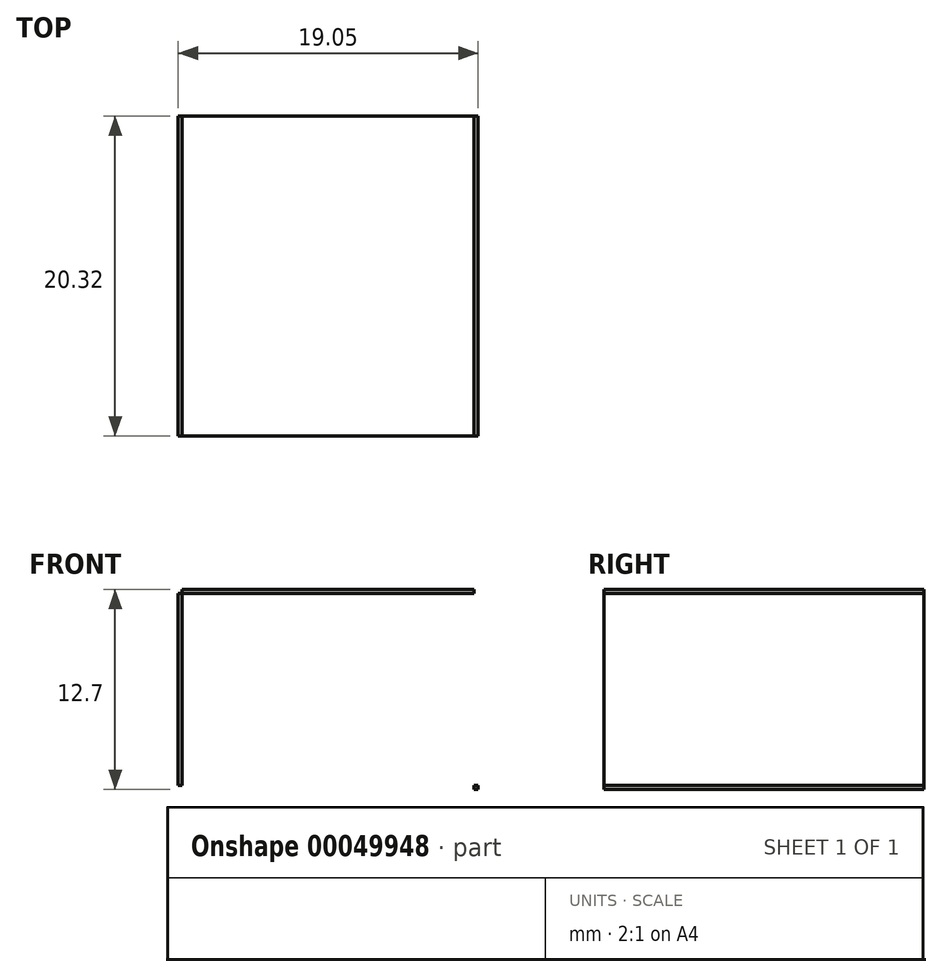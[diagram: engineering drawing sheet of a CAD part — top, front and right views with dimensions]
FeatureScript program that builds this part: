
annotation { "Feature Type Name" : "Feature", "Feature Type Description" : "" }
export const myFeature = defineFeature(function(context is Context, id is Id, definition is map)
    precondition{}
    {
        {
            var Q0;
            Q0=qCreatedBy(makeId("Front.planeOp"),FACE);
            var sketch = newSketch(context, id + "F0", { "sketchPlane" : qUnion([Q0])});
            skLineSegment(sketch, "E0", {"start": v(0, 0) * mm, "end": v(19.05, 0) * mm});
            skLineSegment(sketch, "E1", {"start": v(19.05, 0) * mm, "end": v(19.05, 12.7) * mm});
            skLineSegment(sketch, "E2", {"start": v(19.05, 12.7) * mm, "end": v(0, 12.7) * mm});
            skLineSegment(sketch, "E3", {"start": v(0, 12.7) * mm, "end": v(0, 0) * mm});
            skLineSegment(sketch, "E4", {"start": v(0, 0) * mm, "end": v(0.25, 0) * mm});
            skLineSegment(sketch, "E5", {"start": v(0.25, 0) * mm, "end": v(0.25, 0.25) * mm});
            skLineSegment(sketch, "E6", {"start": v(0.25, 0.25) * mm, "end": v(0, 0.25) * mm});
            skLineSegment(sketch, "E7", {"start": v(0, 12.7) * mm, "end": v(0, 12.45) * mm});
            skLineSegment(sketch, "E8", {"start": v(0, 12.45) * mm, "end": v(0.25, 12.45) * mm});
            skLineSegment(sketch, "E9", {"start": v(0.25, 12.45) * mm, "end": v(0.25, 12.7) * mm});
            skLineSegment(sketch, "E10", {"start": v(0.25, 12.45) * mm, "end": v(0.25, 0.25) * mm});
            skLineSegment(sketch, "E11", {"start": v(19.05, 12.7) * mm, "end": v(18.8, 12.7) * mm});
            skLineSegment(sketch, "E12", {"start": v(18.8, 12.7) * mm, "end": v(18.8, 12.45) * mm});
            skLineSegment(sketch, "E13", {"start": v(18.8, 12.45) * mm, "end": v(0.25, 12.45) * mm});
            skLineSegment(sketch, "E14", {"start": v(19.05, 0.25) * mm, "end": v(18.8, 0.25) * mm});
            skLineSegment(sketch, "E15", {"start": v(18.8, 0.25) * mm, "end": v(18.8, 0) * mm});
            skLineSegment(sketch, "E16", {"start": v(18.8, 0.25) * mm, "end": v(18.8, 12.45) * mm});
            skSolve(sketch);
        }
        {
            var Q0;
            {var subQ4=sQuery(id+"F0.wireOp",EDGE,"E14");Q0=makeQuery(id+"F0.imprint","IMPRINT",FACE,{"disambiguationData":[TD([[makeQuery(id+"F0.imprint","IMPRINT",EDGE,{"derivedFrom":subQ4}),1.0]])]});}
            var Q1;
            {var subQ0=sQuery(id+"F0.wireOp",EDGE,"E7");Q1=makeQuery(id+"F0.imprint","IMPRINT",FACE,{"disambiguationData":[TD([[makeQuery(id+"F0.imprint","IMPRINT",EDGE,{"derivedFrom":subQ0}),1.0]])]});}
            var Q2;
            {var subQ0=sQuery(id+"F0.wireOp",EDGE,"E4");Q2=makeQuery(id+"F0.imprint","IMPRINT",FACE,{"disambiguationData":[TD([[makeQuery(id+"F0.imprint","IMPRINT",EDGE,{"derivedFrom":subQ0}),1.0]])]});}
            var Q3;
            {var subQ0=sQuery(id+"F0.wireOp",EDGE,"E11");Q3=makeQuery(id+"F0.imprint","IMPRINT",FACE,{"disambiguationData":[TD([[makeQuery(id+"F0.imprint","IMPRINT",EDGE,{"derivedFrom":subQ0}),1.0]])]});}
            var Q4;
            {var subQ2=sQuery(id+"F0.wireOp",EDGE,"E9");Q4=makeQuery(id+"F0.imprint","IMPRINT",FACE,{"disambiguationData":[TD([[makeQuery(id+"F0.imprint","IMPRINT",EDGE,{"derivedFrom":subQ2}),-1.0]])]});}
            var Q5;
            {var subQ2=sQuery(id+"F0.wireOp",EDGE,"E6");Q5=makeQuery(id+"F0.imprint","IMPRINT",FACE,{"disambiguationData":[TD([[makeQuery(id+"F0.imprint","IMPRINT",EDGE,{"derivedFrom":subQ2}),-1.0]])]});}
            extrude(context, id + "F1", {"entities" : qUnion([Q0, Q1, Q2, Q3, Q4, Q5]), "depth" : 20.32 * mm});
        }
    });
